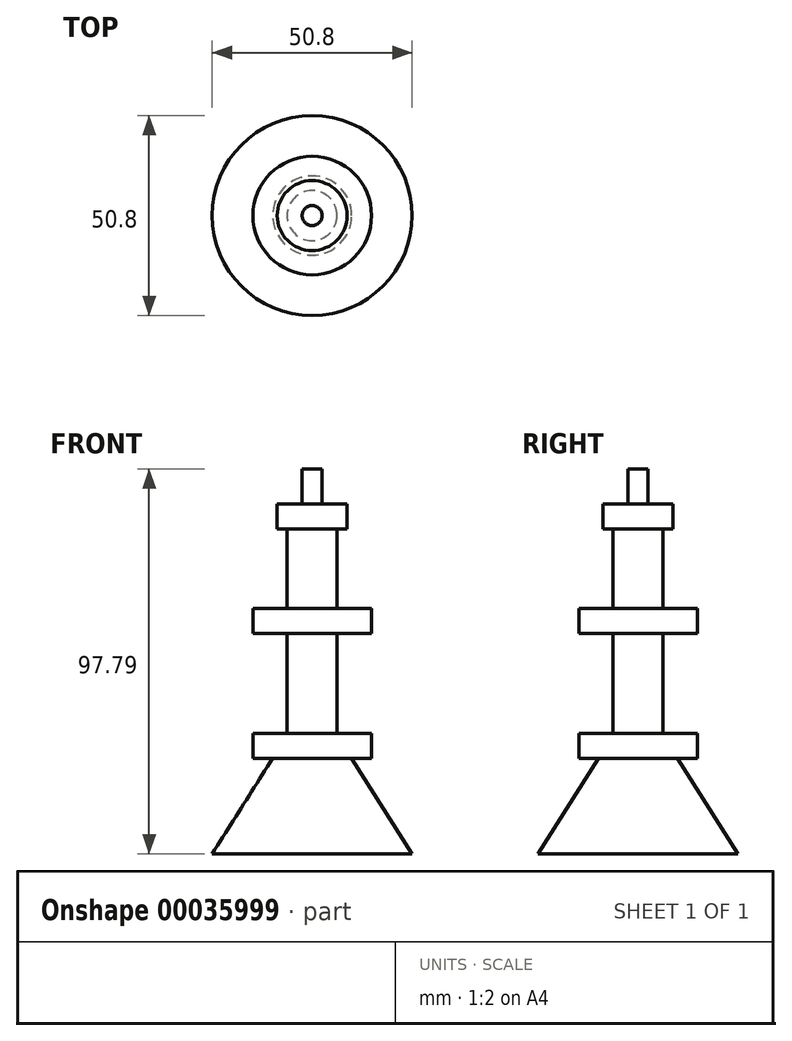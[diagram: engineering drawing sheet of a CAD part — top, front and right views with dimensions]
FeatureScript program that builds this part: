
annotation { "Feature Type Name" : "Feature", "Feature Type Description" : "" }
export const myFeature = defineFeature(function(context is Context, id is Id, definition is map)
    precondition{}
    {
        {
            var Q0;
            Q0=qCreatedBy(makeId("Front.planeOp"),FACE);
            var sketch = newSketch(context, id + "F0", { "sketchPlane" : qUnion([Q0])});
            skLineSegment(sketch, "E0", {"start": v(0, 0) * mm, "end": v(0, 36.7) * mm});
            skLineSegment(sketch, "E1", {"start": v(6.35, 30.35) * mm, "end": v(6.35, 10.19) * mm});
            skLineSegment(sketch, "E2", {"start": v(6.35, 10.19) * mm, "end": v(15.07, 10.19) * mm});
            skLineSegment(sketch, "E3", {"start": v(15.07, 10.19) * mm, "end": v(15.07, 3.84) * mm});
            skLineSegment(sketch, "E4", {"start": v(15.07, 3.84) * mm, "end": v(6.35, 3.84) * mm});
            skLineSegment(sketch, "E5", {"start": v(6.35, 3.84) * mm, "end": v(6.35, -21.56) * mm});
            skLineSegment(sketch, "E6", {"start": v(6.35, -21.56) * mm, "end": v(15.07, -21.56) * mm});
            skLineSegment(sketch, "E7", {"start": v(15.07, -21.56) * mm, "end": v(15.07, -27.91) * mm});
            skLineSegment(sketch, "E8", {"start": v(15.07, -27.91) * mm, "end": v(10.05, -27.91) * mm});
            skLineSegment(sketch, "E9", {"start": v(10.05, -27.91) * mm, "end": v(25.4, -52.2) * mm});
            skLineSegment(sketch, "E10", {"start": v(25.4, -52.2) * mm, "end": v(0, -52.2) * mm});
            skLineSegment(sketch, "E11", {"start": v(0, -52.2) * mm, "end": v(0, 0) * mm});
            skLineSegment(sketch, "E12", {"start": v(6.35, 36.7) * mm, "end": v(8.89, 36.7) * mm});
            skLineSegment(sketch, "E13", {"start": v(8.89, 36.7) * mm, "end": v(8.89, 30.35) * mm});
            skLineSegment(sketch, "E14", {"start": v(8.89, 30.35) * mm, "end": v(6.35, 30.35) * mm});
            skLineSegment(sketch, "E15.top", {"start": v(0, 45.6) * mm, "end": v(2.54, 45.6) * mm});
            skLineSegment(sketch, "E15.left", {"start": v(0, 36.7) * mm, "end": v(0, 45.6) * mm});
            skLineSegment(sketch, "E16.left", {"start": v(0, 45.6) * mm, "end": v(0, 36.7) * mm});
            skLineSegment(sketch, "E16.right", {"start": v(2.54, 45.6) * mm, "end": v(2.54, 36.7) * mm});
            skLineSegment(sketch, "E17", {"start": v(2.54, 36.7) * mm, "end": v(6.35, 36.7) * mm});
            skPoint(sketch, "E18.orphan", {"position": v(6.35, 45.6) * mm});
            skSolve(sketch);
        }
        {
            var Q0;
            Q0=makeQuery(id+"F0.imprint","IMPRINT",FACE,{"disambiguationData":[TD([[makeQuery(id+"F0.imprint","IMPRINT",EDGE,{"derivedFrom":sQuery(id+"F0.wireOp",EDGE,"E0")}),-1.0]])]});
            var Q1;
            Q1=sQuery(id+"F0.wireOp",EDGE,"E0");
            revolve(context, id + "F1", {"entities" : qUnion([Q0]), "axis" : qUnion([Q1]), "revolveType" : RevolveType.FULL});
        }
    });
